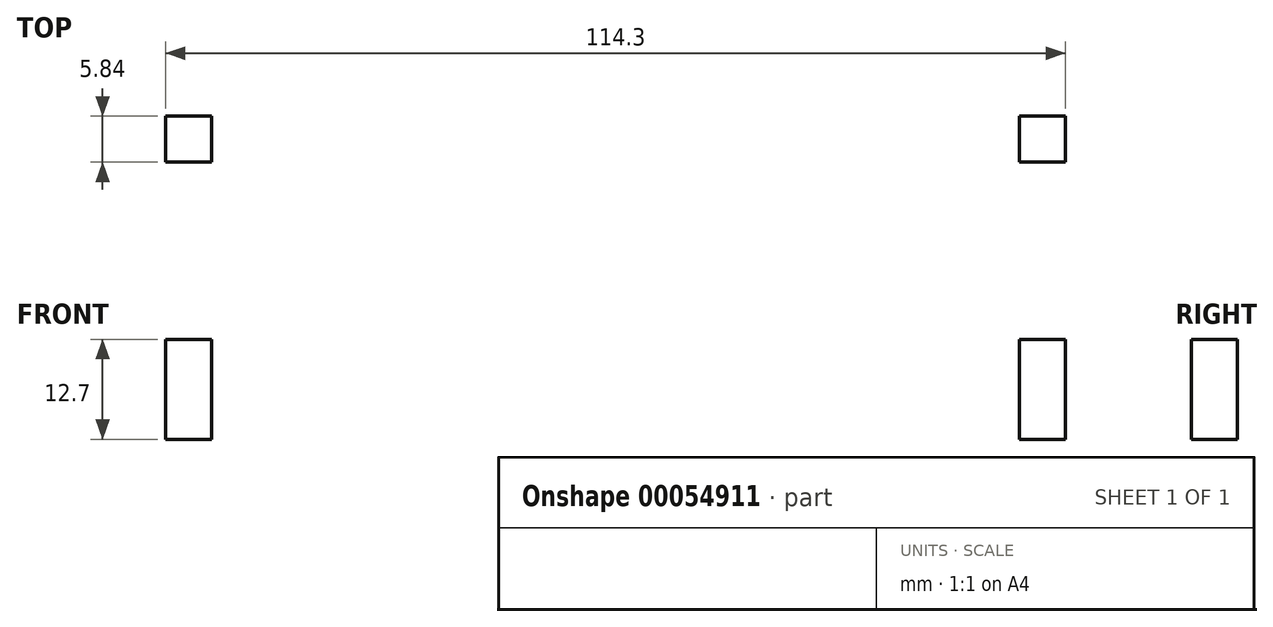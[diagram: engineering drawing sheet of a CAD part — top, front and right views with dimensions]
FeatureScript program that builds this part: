
annotation { "Feature Type Name" : "Feature", "Feature Type Description" : "" }
export const myFeature = defineFeature(function(context is Context, id is Id, definition is map)
    precondition{}
    {
        {
            var Q0;
            Q0=qCreatedBy(makeId("Front.planeOp"),FACE);
            var sketch = newSketch(context, id + "F0", { "sketchPlane" : qUnion([Q0])});
            skLineSegment(sketch, "E0.bottom", {"start": v(-89.92, 0) * mm, "end": v(12.7, 0) * mm});
            skLineSegment(sketch, "E0.top", {"start": v(-89.92, -22.86) * mm, "end": v(12.7, -22.86) * mm});
            skLineSegment(sketch, "E0.left", {"start": v(-89.92, 0) * mm, "end": v(-89.92, -22.86) * mm});
            skLineSegment(sketch, "E0.right", {"start": v(12.7, 0) * mm, "end": v(12.7, -22.86) * mm});
            skLineSegment(sketch, "E1.bottom", {"start": v(-77.22, -22.86) * mm, "end": v(-64, -22.86) * mm});
            skLineSegment(sketch, "E1.top", {"start": v(-77.22, -25.4) * mm, "end": v(-64, -25.4) * mm});
            skLineSegment(sketch, "E1.left", {"start": v(-77.22, -22.86) * mm, "end": v(-77.22, -25.4) * mm});
            skLineSegment(sketch, "E1.right", {"start": v(-64, -22.86) * mm, "end": v(-64, -25.4) * mm});
            skLineSegment(sketch, "E2.bottom", {"start": v(-13.2, -22.86) * mm, "end": v(0, -22.86) * mm});
            skLineSegment(sketch, "E2.top", {"start": v(-13.2, -25.4) * mm, "end": v(0, -25.4) * mm});
            skLineSegment(sketch, "E2.left", {"start": v(-13.2, -22.86) * mm, "end": v(-13.2, -25.4) * mm});
            skLineSegment(sketch, "E2.right", {"start": v(0, -22.86) * mm, "end": v(0, -25.4) * mm});
            skLineSegment(sketch, "E3.bottom", {"start": v(-89.92, -19.05) * mm, "end": v(-95.76, -19.05) * mm});
            skLineSegment(sketch, "E3.top", {"start": v(-89.92, -6.35) * mm, "end": v(-95.76, -6.35) * mm});
            skLineSegment(sketch, "E3.left", {"start": v(-89.92, -19.05) * mm, "end": v(-89.92, -6.35) * mm});
            skLineSegment(sketch, "E3.right", {"start": v(-95.76, -19.05) * mm, "end": v(-95.76, -6.35) * mm});
            skLineSegment(sketch, "E4.bottom", {"start": v(12.7, -19.05) * mm, "end": v(18.54, -19.05) * mm});
            skLineSegment(sketch, "E4.top", {"start": v(12.7, -6.35) * mm, "end": v(18.54, -6.35) * mm});
            skLineSegment(sketch, "E4.left", {"start": v(12.7, -19.05) * mm, "end": v(12.7, -6.35) * mm});
            skLineSegment(sketch, "E4.right", {"start": v(18.54, -19.05) * mm, "end": v(18.54, -6.35) * mm});
            skFitSpline(sketch, "E5", {"points": [v(-89.92, 0) * mm, v(-12.7, 31.75) * mm, v(12.7, 0) * mm], "startDerivative": vector(161.72, 64.69) * mm, "endDerivative": vector(23.17, -139.04) * mm});
            skLineSegment(sketch, "E6", {"start": v(-89.92, -6.35) * mm, "end": v(12.7, -6.35) * mm});
            skSolve(sketch);
        }
        {
            var Q0;
            Q0=makeQuery(id+"F0.imprint","IMPRINT",FACE,{"disambiguationData":[TD([[makeQuery(id+"F0.imprint","IMPRINT",EDGE,{"derivedFrom":sQuery(id+"F0.wireOp",EDGE,"E1.bottom")}),-1.0]])]});
            var Q1;
            Q1=makeQuery(id+"F0.imprint","IMPRINT",FACE,{"disambiguationData":[TD([[makeQuery(id+"F0.imprint","IMPRINT",EDGE,{"derivedFrom":sQuery(id+"F0.wireOp",EDGE,"E2.bottom")}),-1.0]])]});
            var Q2;
            Q2=makeQuery(id+"F0.imprint","IMPRINT",FACE,{"disambiguationData":[TD([[makeQuery(id+"F0.imprint","IMPRINT",EDGE,{"derivedFrom":sQuery(id+"F0.wireOp",EDGE,"E3.bottom")}),-1.0]])]});
            var Q3;
            Q3=makeQuery(id+"F0.imprint","IMPRINT",FACE,{"disambiguationData":[TD([[makeQuery(id+"F0.imprint","IMPRINT",EDGE,{"derivedFrom":sQuery(id+"F0.wireOp",EDGE,"E4.bottom")}),1.0]])]});
            var Q4;
            {var subQ7=sQuery(id+"F0.wireOp",EDGE,"E1.bottom");Q4=makeQuery(id+"F0.imprint","IMPRINT",FACE,{"disambiguationData":[TD([[makeQuery(id+"F0.imprint","IMPRINT",EDGE,{"derivedFrom":subQ7}),1.0]])]});}
            extrude(context, id + "F1", {"entities" : qUnion([Q0, Q1, Q2, Q3, Q4]), "oppositeDirection" : true, "depth" : 5.84 * mm});
        }
    });
